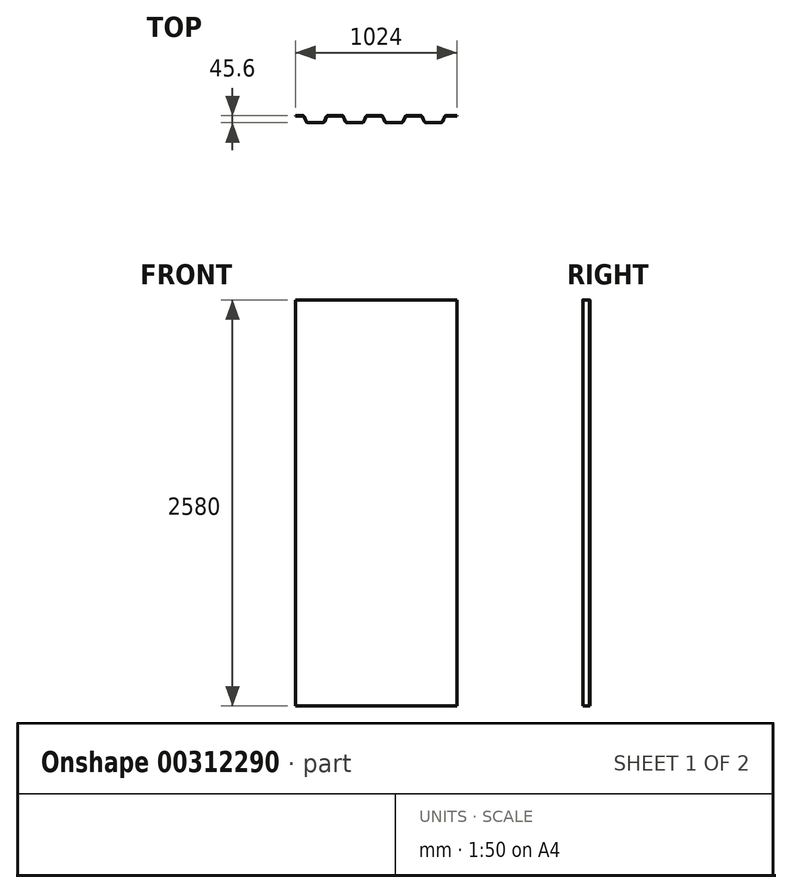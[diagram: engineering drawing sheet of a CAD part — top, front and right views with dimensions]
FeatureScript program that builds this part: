
annotation { "Feature Type Name" : "Feature", "Feature Type Description" : "" }
export const myFeature = defineFeature(function(context is Context, id is Id, definition is map)
    precondition{}
    {
        {
            var Q0;
            Q0=qCreatedBy(makeId("Top.planeOp"),FACE);
            var sketch = newSketch(context, id + "F0", { "sketchPlane" : qUnion([Q0])});
            skLineSegment(sketch, "E0", {"start": v(0, 0) * mm, "end": v(52, 0) * mm, "construction": true});
            skLineSegment(sketch, "E1", {"start": v(52, 0) * mm, "end": v(70, 0) * mm, "construction": true});
            skLineSegment(sketch, "E2", {"start": v(70, 0) * mm, "end": v(180, 0) * mm, "construction": true});
            skLineSegment(sketch, "E3", {"start": v(180, 0) * mm, "end": v(198, 0) * mm});
            skLineSegment(sketch, "E4", {"start": v(198, 0) * mm, "end": v(302, 0) * mm, "construction": true});
            skLineSegment(sketch, "E5", {"start": v(302, 0) * mm, "end": v(320, 0) * mm, "construction": true});
            skLineSegment(sketch, "E6", {"start": v(0, 0) * mm, "end": v(0, 45.6) * mm, "construction": true});
            skLineSegment(sketch, "E7", {"start": v(0, 45.6) * mm, "end": v(42.97, 45.6) * mm});
            skLineSegment(sketch, "E8", {"start": v(55.45, 37.25) * mm, "end": v(66.55, 10.35) * mm});
            skLineSegment(sketch, "E9", {"start": v(79.03, 2) * mm, "end": v(170.97, 2) * mm});
            skLineSegment(sketch, "E10", {"start": v(183.45, 10.35) * mm, "end": v(194.55, 37.25) * mm});
            skLineSegment(sketch, "E11", {"start": v(207.03, 45.6) * mm, "end": v(292.97, 45.6) * mm});
            skLineSegment(sketch, "E12", {"start": v(305.45, 37.25) * mm, "end": v(316.55, 10.35) * mm});
            skLineSegment(sketch, "E13", {"start": v(320, 2) * mm, "end": v(320, 0) * mm, "construction": true});
            skLineSegment(sketch, "E14", {"start": v(430, 0) * mm, "end": v(320, 0) * mm, "construction": true});
            skLineSegment(sketch, "E15", {"start": v(430, 0) * mm, "end": v(448, 0) * mm, "construction": true});
            skLineSegment(sketch, "E16", {"start": v(448, 0) * mm, "end": v(552, 0) * mm, "construction": true});
            skLineSegment(sketch, "E17", {"start": v(552, 0) * mm, "end": v(570, 0) * mm, "construction": true});
            skLineSegment(sketch, "E18", {"start": v(570, 0) * mm, "end": v(680, 0) * mm, "construction": true});
            skLineSegment(sketch, "E19", {"start": v(680, 0) * mm, "end": v(698, 0) * mm, "construction": true});
            skLineSegment(sketch, "E20", {"start": v(698, 0) * mm, "end": v(802, 0) * mm, "construction": true});
            skLineSegment(sketch, "E21", {"start": v(802, 0) * mm, "end": v(820, 0) * mm, "construction": true});
            skLineSegment(sketch, "E22", {"start": v(820, 0) * mm, "end": v(930, 0) * mm, "construction": true});
            skLineSegment(sketch, "E23", {"start": v(329.03, 2) * mm, "end": v(420.97, 2) * mm});
            skLineSegment(sketch, "E24", {"start": v(433.45, 10.35) * mm, "end": v(444.55, 37.25) * mm});
            skLineSegment(sketch, "E25", {"start": v(457.03, 45.6) * mm, "end": v(542.97, 45.6) * mm});
            skLineSegment(sketch, "E26", {"start": v(555.45, 37.25) * mm, "end": v(566.55, 10.35) * mm});
            skLineSegment(sketch, "E27", {"start": v(579.03, 2) * mm, "end": v(670.97, 2) * mm});
            skLineSegment(sketch, "E28", {"start": v(683.45, 10.35) * mm, "end": v(694.55, 37.25) * mm});
            skLineSegment(sketch, "E29", {"start": v(707.03, 45.6) * mm, "end": v(792.97, 45.6) * mm});
            skLineSegment(sketch, "E30", {"start": v(805.45, 37.25) * mm, "end": v(816.55, 10.35) * mm});
            skLineSegment(sketch, "E31", {"start": v(829.03, 2) * mm, "end": v(920.97, 2) * mm});
            skLineSegment(sketch, "E32", {"start": v(930, 0) * mm, "end": v(948, 0) * mm, "construction": true});
            skLineSegment(sketch, "E33", {"start": v(948, 0) * mm, "end": v(1024, 0) * mm, "construction": true});
            skLineSegment(sketch, "E34", {"start": v(933.45, 10.35) * mm, "end": v(944.55, 37.25) * mm});
            skLineSegment(sketch, "E35", {"start": v(957.03, 45.6) * mm, "end": v(1024, 45.6) * mm});
            skPoint(sketch, "E36.visualSharp", {"position": v(930, 2) * mm});
            skArc(sketch, "E36.filletArc", {"start": v(920.97, 2) * mm, "mid": v(928.47, 4.28) * mm, "end": v(933.45, 10.35) * mm});
            skPoint(sketch, "E37.visualSharp", {"position": v(948, 45.6) * mm});
            skArc(sketch, "E37.filletArc", {"start": v(957.03, 45.6) * mm, "mid": v(949.53, 43.32) * mm, "end": v(944.55, 37.25) * mm});
            skPoint(sketch, "E38.visualSharp", {"position": v(802, 45.6) * mm});
            skArc(sketch, "E38.filletArc", {"start": v(805.45, 37.25) * mm, "mid": v(800.47, 43.32) * mm, "end": v(792.97, 45.6) * mm});
            skPoint(sketch, "E39.visualSharp", {"position": v(820, 2) * mm});
            skArc(sketch, "E39.filletArc", {"start": v(816.55, 10.35) * mm, "mid": v(821.53, 4.28) * mm, "end": v(829.03, 2) * mm});
            skPoint(sketch, "E40.visualSharp", {"position": v(698, 45.6) * mm});
            skArc(sketch, "E40.filletArc", {"start": v(707.03, 45.6) * mm, "mid": v(699.53, 43.32) * mm, "end": v(694.55, 37.25) * mm});
            skPoint(sketch, "E41.visualSharp", {"position": v(680, 2) * mm});
            skArc(sketch, "E41.filletArc", {"start": v(670.97, 2) * mm, "mid": v(678.47, 4.28) * mm, "end": v(683.45, 10.35) * mm});
            skPoint(sketch, "E42.visualSharp", {"position": v(552, 45.6) * mm});
            skArc(sketch, "E42.filletArc", {"start": v(555.45, 37.25) * mm, "mid": v(550.47, 43.32) * mm, "end": v(542.97, 45.6) * mm});
            skPoint(sketch, "E43.visualSharp", {"position": v(570, 2) * mm});
            skArc(sketch, "E43.filletArc", {"start": v(566.55, 10.35) * mm, "mid": v(571.53, 4.28) * mm, "end": v(579.03, 2) * mm});
            skPoint(sketch, "E44.visualSharp", {"position": v(448, 45.6) * mm});
            skArc(sketch, "E44.filletArc", {"start": v(457.03, 45.6) * mm, "mid": v(449.53, 43.32) * mm, "end": v(444.55, 37.25) * mm});
            skPoint(sketch, "E45.visualSharp", {"position": v(430, 2) * mm});
            skArc(sketch, "E45.filletArc", {"start": v(420.97, 2) * mm, "mid": v(428.47, 4.28) * mm, "end": v(433.45, 10.35) * mm});
            skPoint(sketch, "E46.visualSharp", {"position": v(320, 2) * mm});
            skArc(sketch, "E46.filletArc", {"start": v(316.55, 10.35) * mm, "mid": v(321.53, 4.28) * mm, "end": v(329.03, 2) * mm});
            skPoint(sketch, "E47.visualSharp", {"position": v(302, 45.6) * mm});
            skArc(sketch, "E47.filletArc", {"start": v(305.45, 37.25) * mm, "mid": v(300.47, 43.32) * mm, "end": v(292.97, 45.6) * mm});
            skPoint(sketch, "E48.visualSharp", {"position": v(198, 45.6) * mm});
            skArc(sketch, "E48.filletArc", {"start": v(207.03, 45.6) * mm, "mid": v(199.53, 43.32) * mm, "end": v(194.55, 37.25) * mm});
            skPoint(sketch, "E49.visualSharp", {"position": v(180, 2) * mm});
            skArc(sketch, "E49.filletArc", {"start": v(170.97, 2) * mm, "mid": v(178.47, 4.28) * mm, "end": v(183.45, 10.35) * mm});
            skPoint(sketch, "E50.visualSharp", {"position": v(70, 2) * mm});
            skArc(sketch, "E50.filletArc", {"start": v(66.55, 10.35) * mm, "mid": v(71.53, 4.28) * mm, "end": v(79.03, 2) * mm});
            skPoint(sketch, "E51.visualSharp", {"position": v(52, 45.6) * mm});
            skArc(sketch, "E51.filletArc", {"start": v(55.45, 37.25) * mm, "mid": v(50.47, 43.32) * mm, "end": v(42.97, 45.6) * mm});
            skArc(sketch, "E52.0", {"start": v(920.97, 0) * mm, "mid": v(929.59, 2.62) * mm, "end": v(935.3, 9.59) * mm});
            skLineSegment(sketch, "E52.1", {"start": v(829.03, 0) * mm, "end": v(920.97, 0) * mm});
            skArc(sketch, "E52.2", {"start": v(814.7, 9.59) * mm, "mid": v(820.41, 2.62) * mm, "end": v(829.03, 0) * mm});
            skLineSegment(sketch, "E52.3", {"start": v(803.6, 36.49) * mm, "end": v(814.7, 9.59) * mm});
            skArc(sketch, "E52.4", {"start": v(803.6, 36.49) * mm, "mid": v(799.36, 41.66) * mm, "end": v(792.97, 43.6) * mm});
            skLineSegment(sketch, "E52.5", {"start": v(707.03, 43.6) * mm, "end": v(792.97, 43.6) * mm});
            skArc(sketch, "E52.6", {"start": v(707.03, 43.6) * mm, "mid": v(700.64, 41.66) * mm, "end": v(696.4, 36.49) * mm});
            skLineSegment(sketch, "E52.7", {"start": v(685.3, 9.59) * mm, "end": v(696.4, 36.49) * mm});
            skArc(sketch, "E52.8", {"start": v(303.6, 36.49) * mm, "mid": v(299.36, 41.66) * mm, "end": v(292.97, 43.6) * mm});
            skLineSegment(sketch, "E52.9", {"start": v(207.03, 43.6) * mm, "end": v(292.97, 43.6) * mm});
            skArc(sketch, "E52.10", {"start": v(207.03, 43.6) * mm, "mid": v(200.64, 41.66) * mm, "end": v(196.4, 36.49) * mm});
            skLineSegment(sketch, "E52.11", {"start": v(185.3, 9.59) * mm, "end": v(196.4, 36.49) * mm});
            skArc(sketch, "E52.12", {"start": v(170.97, 0) * mm, "mid": v(179.59, 2.62) * mm, "end": v(185.3, 9.59) * mm});
            skLineSegment(sketch, "E52.13", {"start": v(79.03, 0) * mm, "end": v(170.97, 0) * mm});
            skLineSegment(sketch, "E52.14", {"start": v(0, 43.6) * mm, "end": v(42.97, 43.6) * mm});
            skArc(sketch, "E52.15", {"start": v(53.6, 36.49) * mm, "mid": v(49.36, 41.66) * mm, "end": v(42.97, 43.6) * mm});
            skLineSegment(sketch, "E52.16", {"start": v(53.6, 36.49) * mm, "end": v(64.7, 9.59) * mm});
            skArc(sketch, "E52.17", {"start": v(64.7, 9.59) * mm, "mid": v(70.41, 2.62) * mm, "end": v(79.03, 0) * mm});
            skLineSegment(sketch, "E52.18", {"start": v(303.6, 36.49) * mm, "end": v(314.7, 9.59) * mm});
            skArc(sketch, "E52.19", {"start": v(314.7, 9.59) * mm, "mid": v(320.41, 2.62) * mm, "end": v(329.03, 0) * mm});
            skLineSegment(sketch, "E52.20", {"start": v(329.03, 0) * mm, "end": v(420.97, 0) * mm});
            skArc(sketch, "E52.21", {"start": v(420.97, 0) * mm, "mid": v(429.59, 2.62) * mm, "end": v(435.3, 9.59) * mm});
            skLineSegment(sketch, "E52.22", {"start": v(435.3, 9.59) * mm, "end": v(446.4, 36.49) * mm});
            skArc(sketch, "E52.23", {"start": v(457.03, 43.6) * mm, "mid": v(450.64, 41.66) * mm, "end": v(446.4, 36.49) * mm});
            skLineSegment(sketch, "E52.24", {"start": v(457.03, 43.6) * mm, "end": v(542.97, 43.6) * mm});
            skArc(sketch, "E52.25", {"start": v(553.6, 36.49) * mm, "mid": v(549.36, 41.66) * mm, "end": v(542.97, 43.6) * mm});
            skLineSegment(sketch, "E52.26", {"start": v(553.6, 36.49) * mm, "end": v(564.7, 9.59) * mm});
            skArc(sketch, "E52.27", {"start": v(564.7, 9.59) * mm, "mid": v(570.41, 2.62) * mm, "end": v(579.03, 0) * mm});
            skLineSegment(sketch, "E52.28", {"start": v(579.03, 0) * mm, "end": v(670.97, 0) * mm});
            skArc(sketch, "E52.29", {"start": v(670.97, 0) * mm, "mid": v(679.59, 2.62) * mm, "end": v(685.3, 9.59) * mm});
            skLineSegment(sketch, "E53.0", {"start": v(957.03, 43.6) * mm, "end": v(1024, 43.6) * mm});
            skArc(sketch, "E53.1", {"start": v(957.03, 43.6) * mm, "mid": v(950.64, 41.66) * mm, "end": v(946.4, 36.49) * mm});
            skLineSegment(sketch, "E53.2", {"start": v(935.3, 9.59) * mm, "end": v(946.4, 36.49) * mm});
            skLineSegment(sketch, "E54", {"start": v(1024, 45.6) * mm, "end": v(1024, 43.6) * mm});
            skLineSegment(sketch, "E55", {"start": v(0, 45.6) * mm, "end": v(0, 43.6) * mm});
            skSolve(sketch);
        }
        {
            var Q0;
            Q0 = qSketchRegion(id + "F0", true);
            extrude(context, id + "F1", {"entities" : qUnion([Q0]), "depth" : 2580 * mm});
        }
    });
